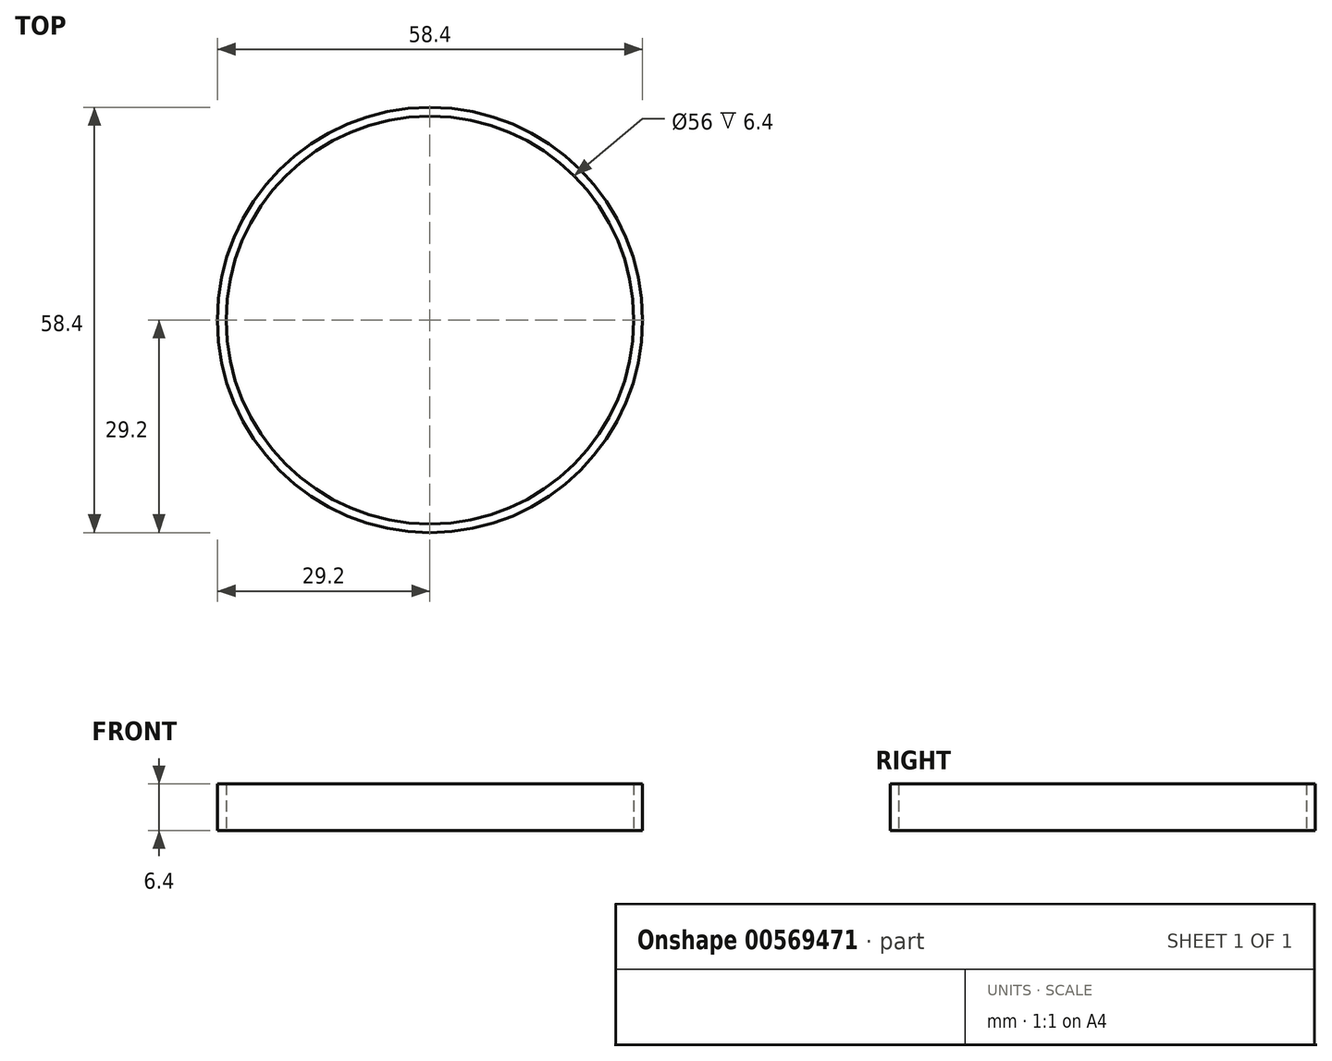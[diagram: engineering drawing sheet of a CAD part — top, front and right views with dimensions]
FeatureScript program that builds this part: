
annotation { "Feature Type Name" : "Feature", "Feature Type Description" : "" }
export const myFeature = defineFeature(function(context is Context, id is Id, definition is map)
    precondition{}
    {
        {
            var Q0;
            Q0=qCreatedBy(makeId("Top.planeOp"),FACE);
            var sketch = newSketch(context, id + "F0", { "sketchPlane" : qUnion([Q0])});
            skCircle(sketch, "E0", {"center": v(0, 0) * mm, "radius": 28 * mm});
            skCircle(sketch, "E1", {"center": v(0, 0) * mm, "radius": 29.2 * mm});
            skSolve(sketch);
        }
        {
            var Q0;
            Q0 = qSketchRegion(id + "F0", true);
            extrude(context, id + "F1", {"entities" : qUnion([Q0]), "depth" : 6.4 * mm, "offsetDistance" : 25 * mm});
        }
    });
